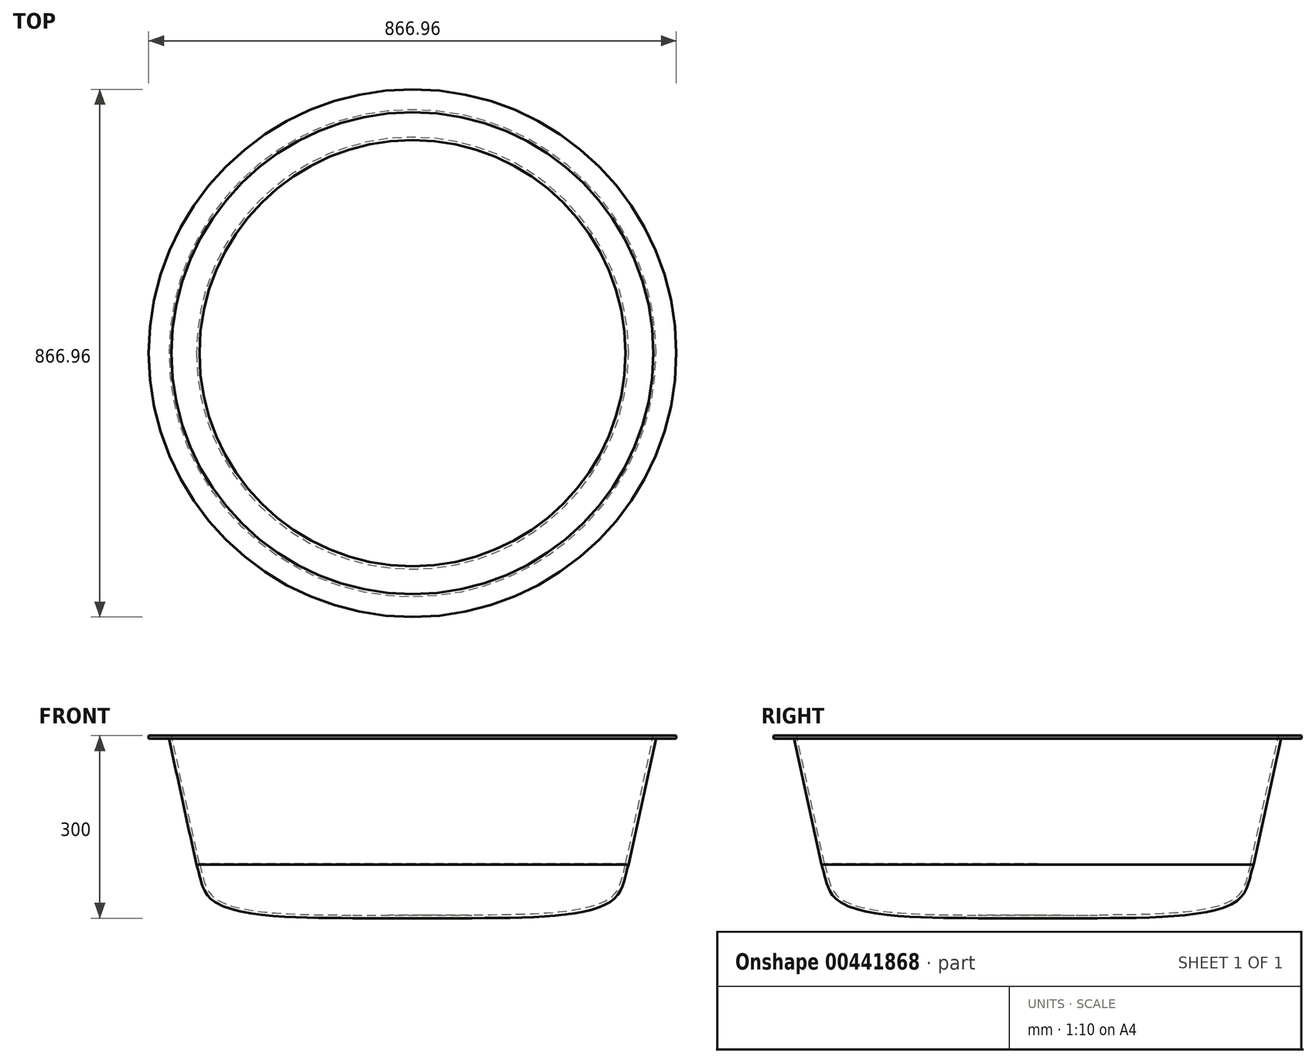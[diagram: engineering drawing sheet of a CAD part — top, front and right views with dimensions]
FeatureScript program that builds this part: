
annotation { "Feature Type Name" : "Feature", "Feature Type Description" : "" }
export const myFeature = defineFeature(function(context is Context, id is Id, definition is map)
    precondition{}
    {
        {
            var Q0;
            Q0=qCreatedBy(makeId("Top.planeOp"),FACE);
            var sketch = newSketch(context, id + "F0", { "sketchPlane" : qUnion([Q0])});
            skCircle(sketch, "E0", {"center": v(0, 0) * mm, "radius": 433.48 * mm});
            skSolve(sketch);
        }
        {
            var Q0;
            Q0=makeQuery(id+"F0.imprint","IMPRINT",FACE,{"disambiguationData":[TD([[makeQuery(id+"F0.imprint","IMPRINT",EDGE,{"derivedFrom":sQuery(id+"F0.wireOp",EDGE,"E0")}),1.0]])]});
            extrude(context, id + "F1", {"entities" : qUnion([Q0]), "oppositeDirection" : true, "depth" : 300 * mm});
        }
        {
            var Q0;
            Q0=qCreatedBy(makeId("Front.planeOp"),FACE);
            var sketch = newSketch(context, id + "F2", { "sketchPlane" : qUnion([Q0])});
            skLineSegment(sketch, "E1", {"start": v(500, -5) * mm, "end": v(400, -5) * mm});
            skLineSegment(sketch, "E2", {"start": v(400, -5) * mm, "end": v(354.9, -212.25) * mm});
            skFitSpline(sketch, "E3", {"points": [v(354.9, -212.25) * mm, v(329.3, -269.85) * mm, v(0, -300) * mm], "startDerivative": vector(-66.37, -170.14) * mm, "endDerivative": vector(-588.8, -5.14) * mm});
            skLineSegment(sketch, "E4", {"start": v(500, -5) * mm, "end": v(500, -413.17) * mm});
            skLineSegment(sketch, "E5", {"start": v(500, -413.17) * mm, "end": v(0, -436.49) * mm});
            skLineSegment(sketch, "E6", {"start": v(0, -436.49) * mm, "end": v(0, -300) * mm});
            skLineSegment(sketch, "E7", {"start": v(0, 0) * mm, "end": v(0, -245.4) * mm, "construction": true});
            skSolve(sketch);
        }
        {
            var Q0;
            Q0 = qSketchRegion(id + "F2", true);
            var Q1;
            Q1=sQuery(id+"F2.wireOp",EDGE,"E7");
            revolve(context, id + "F3", {"operationType" : NewBodyOperationType.REMOVE, "entities" : qUnion([Q0]), "axis" : qUnion([Q1]), "revolveType" : RevolveType.FULL, "oppositeDirection" : true});
        }
        {
            var Q0;
            Q0 = qSketchRegion(id + "F2", true);
            var Q1;
            Q1=sQuery(id+"F2.wireOp",EDGE,"E7");
            revolve(context, id + "F4", {"operationType" : NewBodyOperationType.REMOVE, "entities" : qUnion([Q0]), "axis" : qUnion([Q1]), "revolveType" : RevolveType.FULL, "oppositeDirection" : true});
        }
        {
            var Q0;
            Q0=makeQuery(id+"F1.opExtrude","CAP_FACE",FACE,{"disambiguationData":[OSD([sQuery(id+"F0.wireOp",EDGE,"E0")])],"isStart":true});
            shell(context, id + "F5", {"entities" : qUnion([Q0]), "thickness" : 5 * mm});
        }
    });
